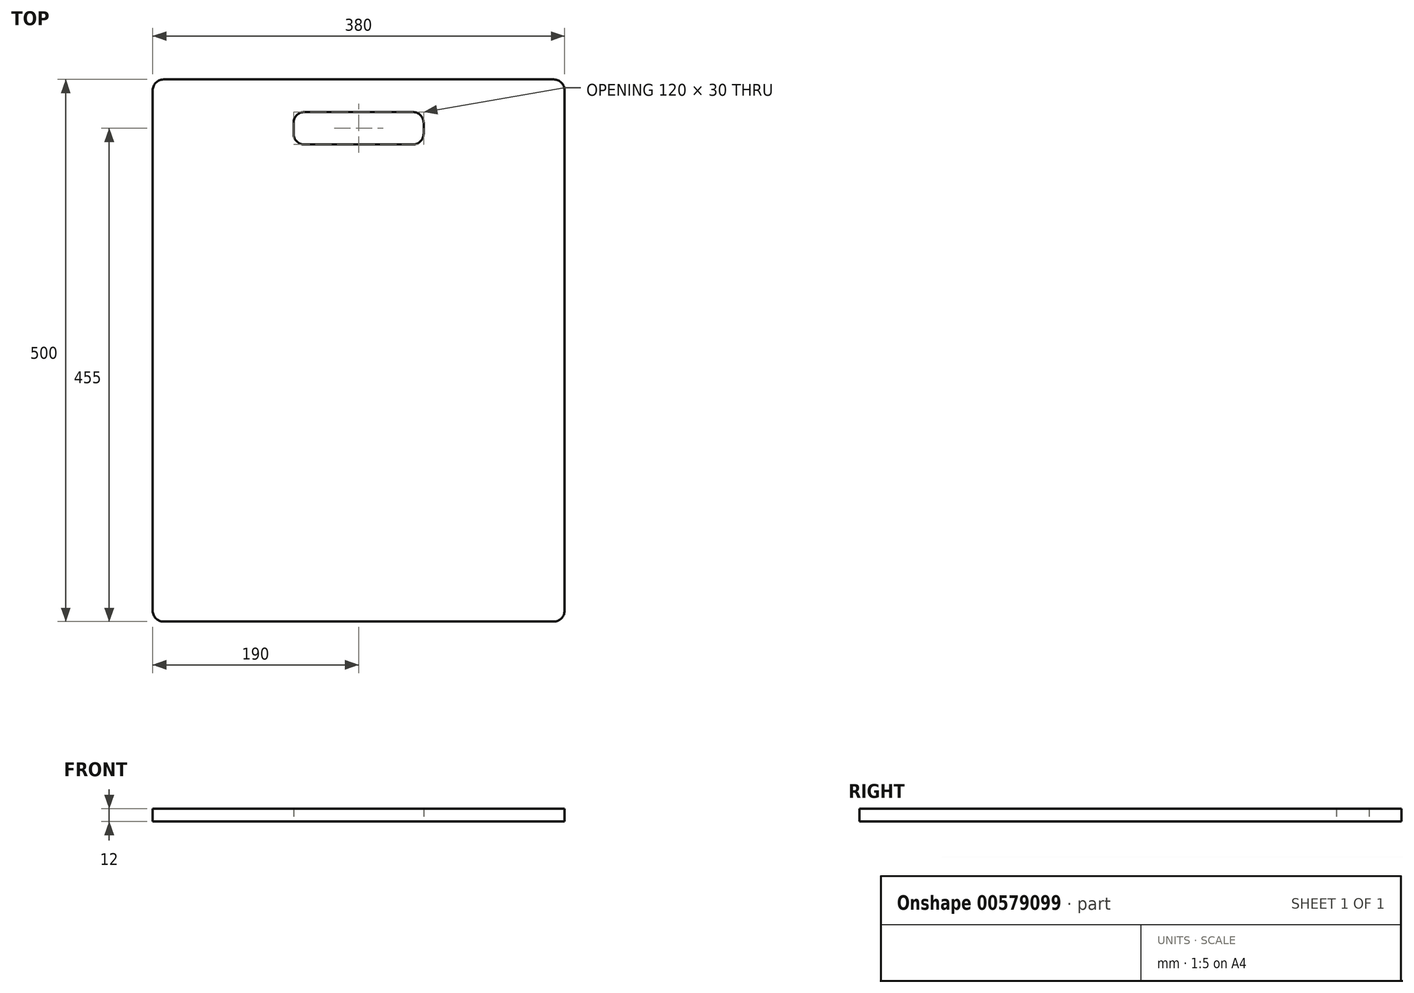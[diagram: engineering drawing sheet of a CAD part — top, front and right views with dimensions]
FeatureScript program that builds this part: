
annotation { "Feature Type Name" : "Feature", "Feature Type Description" : "" }
export const myFeature = defineFeature(function(context is Context, id is Id, definition is map)
    precondition{}
    {
        {
            var Q0;
            Q0=qCreatedBy(makeId("Top.planeOp"),FACE);
            var sketch = newSketch(context, id + "F0", { "sketchPlane" : qUnion([Q0])});
            skLineSegment(sketch, "E0.bottom", {"start": v(190, 250) * mm, "end": v(-190, 250) * mm});
            skLineSegment(sketch, "E0.top", {"start": v(190, -250) * mm, "end": v(-190, -250) * mm});
            skLineSegment(sketch, "E0.left", {"start": v(190, 250) * mm, "end": v(190, -250) * mm});
            skLineSegment(sketch, "E0.right", {"start": v(-190, 250) * mm, "end": v(-190, -250) * mm});
            skPoint(sketch, "E0.middle", {"position": v(0, 0) * mm});
            skLineSegment(sketch, "E1.bottom", {"start": v(-60, 220) * mm, "end": v(60, 220) * mm});
            skLineSegment(sketch, "E1.top", {"start": v(-60, 190) * mm, "end": v(60, 190) * mm});
            skLineSegment(sketch, "E1.left", {"start": v(-60, 220) * mm, "end": v(-60, 190) * mm});
            skLineSegment(sketch, "E1.right", {"start": v(60, 220) * mm, "end": v(60, 190) * mm});
            skLineSegment(sketch, "E2", {"start": v(0, 0) * mm, "end": v(0, 279.36) * mm, "construction": true});
            skSolve(sketch);
        }
        {
            var Q0;
            Q0 = qSketchRegion(id + "F0", true);
            extrude(context, id + "F1", {"entities" : qUnion([Q0]), "depth" : 12 * mm, "offsetDistance" : 25 * mm});
        }
        {
            var Q0;
            Q0=makeQuery(id+"F1.opExtrude","SWEPT_EDGE",EDGE,{"disambiguationData":[OSD([sQuery(id+"F0.wireOp",EDGE,"E0.bottom"),sQuery(id+"F0.wireOp",EDGE,"E0.right")])]});
            var Q1;
            Q1=makeQuery(id+"F1.opExtrude","SWEPT_EDGE",EDGE,{"disambiguationData":[OSD([sQuery(id+"F0.wireOp",EDGE,"E0.bottom"),sQuery(id+"F0.wireOp",EDGE,"E0.left")])]});
            var Q2;
            Q2=makeQuery(id+"F1.opExtrude","SWEPT_EDGE",EDGE,{"disambiguationData":[OSD([sQuery(id+"F0.wireOp",EDGE,"E1.top"),sQuery(id+"F0.wireOp",EDGE,"E1.right")])]});
            var Q3;
            Q3=makeQuery(id+"F1.opExtrude","SWEPT_EDGE",EDGE,{"disambiguationData":[OSD([sQuery(id+"F0.wireOp",EDGE,"E1.bottom"),sQuery(id+"F0.wireOp",EDGE,"E1.right")])]});
            var Q4;
            Q4=makeQuery(id+"F1.opExtrude","SWEPT_EDGE",EDGE,{"disambiguationData":[OSD([sQuery(id+"F0.wireOp",EDGE,"E1.bottom"),sQuery(id+"F0.wireOp",EDGE,"E1.left")])]});
            var Q5;
            Q5=makeQuery(id+"F1.opExtrude","SWEPT_EDGE",EDGE,{"disambiguationData":[OSD([sQuery(id+"F0.wireOp",EDGE,"E1.top"),sQuery(id+"F0.wireOp",EDGE,"E1.left")])]});
            var Q6;
            Q6=makeQuery(id+"F1.opExtrude","SWEPT_EDGE",EDGE,{"disambiguationData":[OSD([sQuery(id+"F0.wireOp",EDGE,"E0.top"),sQuery(id+"F0.wireOp",EDGE,"E0.left")])]});
            var Q7;
            Q7=makeQuery(id+"F1.opExtrude","SWEPT_EDGE",EDGE,{"disambiguationData":[OSD([sQuery(id+"F0.wireOp",EDGE,"E0.top"),sQuery(id+"F0.wireOp",EDGE,"E0.right")])]});
            fillet(context, id + "F2", {"entities" : qUnion([Q0, Q1, Q2, Q3, Q4, Q5, Q6, Q7]), "radius" : 10 * mm, "tangentPropagation" : true, "allowEdgeOverflow" : false});
        }
    });
